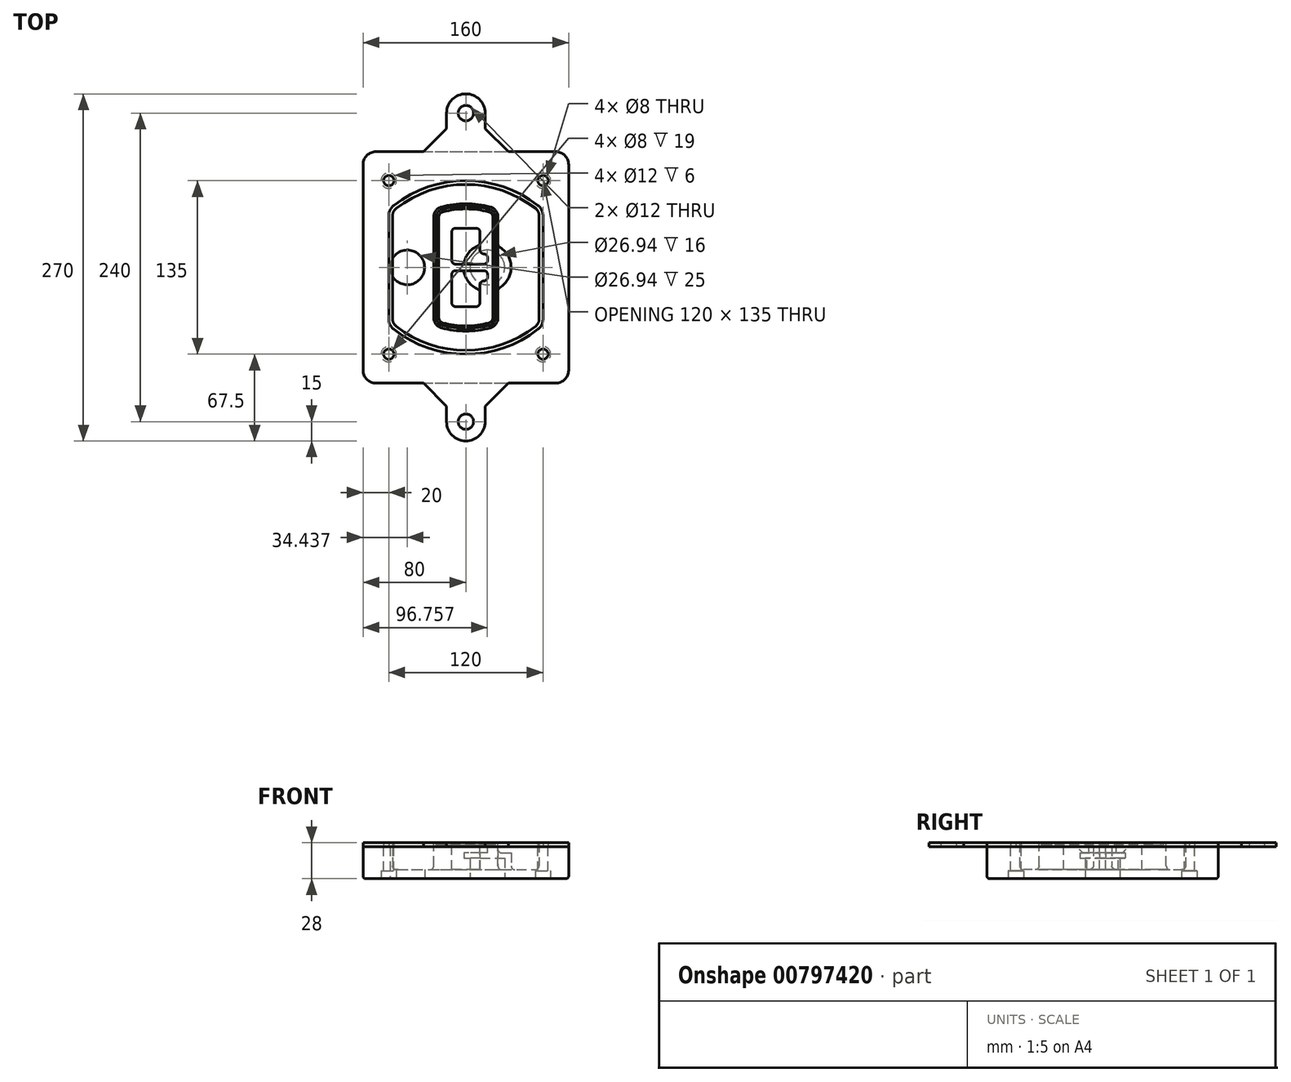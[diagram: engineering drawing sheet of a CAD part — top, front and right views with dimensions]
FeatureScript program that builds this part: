
annotation { "Feature Type Name" : "Feature", "Feature Type Description" : "" }
export const myFeature = defineFeature(function(context is Context, id is Id, definition is map)
    precondition{}
    {
        {
            var Q0;
            Q0=qCreatedBy(makeId("Top.planeOp"),FACE);
            var sketch = newSketch(context, id + "F0", { "sketchPlane" : qUnion([Q0])});
            skPoint(sketch, "E0.rect.middle", {"position": v(0, 0) * mm});
            skLineSegment(sketch, "E1.bottom", {"start": v(-70, -90) * mm, "end": v(70, -90) * mm});
            skLineSegment(sketch, "E1.top", {"start": v(-70, 90) * mm, "end": v(70, 90) * mm});
            skLineSegment(sketch, "E1.left", {"start": v(-80, -80) * mm, "end": v(-80, 80) * mm});
            skLineSegment(sketch, "E1.right", {"start": v(80, -80) * mm, "end": v(80, 80) * mm});
            skLineSegment(sketch, "E2", {"start": v(-80, 90) * mm, "end": v(80, -90) * mm, "construction": true});
            skLineSegment(sketch, "E3", {"start": v(80, 90) * mm, "end": v(-80, -90) * mm, "construction": true});
            skCircle(sketch, "E4", {"center": v(-60, 67.5) * mm, "radius": 4 * mm});
            skCircle(sketch, "E5", {"center": v(60, 67.5) * mm, "radius": 4 * mm});
            skCircle(sketch, "E6", {"center": v(60, -67.5) * mm, "radius": 4 * mm});
            skCircle(sketch, "E7", {"center": v(-60, -67.5) * mm, "radius": 4 * mm});
            skLineSegment(sketch, "E8", {"start": v(-60, 67.5) * mm, "end": v(60, 67.5) * mm, "construction": true});
            skLineSegment(sketch, "E9", {"start": v(60, 67.5) * mm, "end": v(60, -67.5) * mm, "construction": true});
            skLineSegment(sketch, "E10", {"start": v(60, -67.5) * mm, "end": v(-60, -67.5) * mm, "construction": true});
            skLineSegment(sketch, "E11", {"start": v(-60, -67.5) * mm, "end": v(-60, 67.5) * mm, "construction": true});
            skLineSegment(sketch, "E12", {"start": v(-60, 40.3) * mm, "end": v(-60, -40.3) * mm});
            skLineSegment(sketch, "E13", {"start": v(60, 40.3) * mm, "end": v(60, -40.3) * mm});
            skArc(sketch, "E14", {"start": v(56.15, 48.18) * mm, "mid": v(0, 67.5) * mm, "end": v(-56.15, 48.18) * mm});
            skArc(sketch, "E15", {"start": v(-56.15, -48.18) * mm, "mid": v(0, -67.5) * mm, "end": v(56.15, -48.18) * mm});
            skLineSegment(sketch, "E16", {"start": v(-60, 0) * mm, "end": v(60, 0) * mm, "construction": true});
            skPoint(sketch, "E17.visualSharp", {"position": v(-60, -45) * mm});
            skArc(sketch, "E17.filletArc", {"start": v(-60, -40.3) * mm, "mid": v(-58.99, -44.68) * mm, "end": v(-56.15, -48.18) * mm});
            skPoint(sketch, "E18.visualSharp", {"position": v(-60, 45) * mm});
            skArc(sketch, "E18.filletArc", {"start": v(-56.15, 48.18) * mm, "mid": v(-58.99, 44.68) * mm, "end": v(-60, 40.3) * mm});
            skPoint(sketch, "E19.visualSharp", {"position": v(60, 45) * mm});
            skArc(sketch, "E19.filletArc", {"start": v(60, 40.3) * mm, "mid": v(58.99, 44.68) * mm, "end": v(56.15, 48.18) * mm});
            skPoint(sketch, "E20.visualSharp", {"position": v(60, -45) * mm});
            skArc(sketch, "E20.filletArc", {"start": v(56.15, -48.18) * mm, "mid": v(58.99, -44.68) * mm, "end": v(60, -40.3) * mm});
            skPoint(sketch, "E21.visualSharp", {"position": v(-80, 90) * mm});
            skArc(sketch, "E21.filletArc", {"start": v(-70, 90) * mm, "mid": v(-77.07, 87.07) * mm, "end": v(-80, 80) * mm});
            skPoint(sketch, "E22.visualSharp", {"position": v(80, 90) * mm});
            skArc(sketch, "E22.filletArc", {"start": v(80, 80) * mm, "mid": v(77.07, 87.07) * mm, "end": v(70, 90) * mm});
            skPoint(sketch, "E23.visualSharp", {"position": v(80, -90) * mm});
            skArc(sketch, "E23.filletArc", {"start": v(70, -90) * mm, "mid": v(77.07, -87.07) * mm, "end": v(80, -80) * mm});
            skPoint(sketch, "E24.visualSharp", {"position": v(-80, -90) * mm});
            skArc(sketch, "E24.filletArc", {"start": v(-80, -80) * mm, "mid": v(-77.07, -87.07) * mm, "end": v(-70, -90) * mm});
            skArc(sketch, "E25.0", {"start": v(57, 40.3) * mm, "mid": v(56.3, 43.36) * mm, "end": v(54.3, 45.81) * mm});
            skLineSegment(sketch, "E25.1", {"start": v(57, 40.3) * mm, "end": v(57, -40.3) * mm});
            skArc(sketch, "E25.2", {"start": v(54.3, -45.81) * mm, "mid": v(56.3, -43.36) * mm, "end": v(57, -40.3) * mm});
            skArc(sketch, "E25.3", {"start": v(-54.3, -45.81) * mm, "mid": v(0, -64.5) * mm, "end": v(54.3, -45.81) * mm});
            skArc(sketch, "E25.4", {"start": v(-57, -40.3) * mm, "mid": v(-56.3, -43.36) * mm, "end": v(-54.3, -45.81) * mm});
            skArc(sketch, "E25.5", {"start": v(54.3, 45.81) * mm, "mid": v(0, 64.5) * mm, "end": v(-54.3, 45.81) * mm});
            skLineSegment(sketch, "E25.6", {"start": v(-57, 40.3) * mm, "end": v(-57, -40.3) * mm});
            skArc(sketch, "E25.7", {"start": v(-54.3, 45.81) * mm, "mid": v(-56.3, 43.36) * mm, "end": v(-57, 40.3) * mm});
            skArc(sketch, "E26.0", {"start": v(-58.62, 51.33) * mm, "mid": v(-62.58, 46.43) * mm, "end": v(-64, 40.3) * mm});
            skArc(sketch, "E26.1", {"start": v(58.62, 51.33) * mm, "mid": v(0, 71.5) * mm, "end": v(-58.62, 51.33) * mm});
            skArc(sketch, "E26.2", {"start": v(64, 40.3) * mm, "mid": v(62.58, 46.43) * mm, "end": v(58.62, 51.33) * mm});
            skLineSegment(sketch, "E26.3", {"start": v(64, 40.3) * mm, "end": v(64, -40.3) * mm});
            skArc(sketch, "E26.4", {"start": v(58.62, -51.33) * mm, "mid": v(62.58, -46.43) * mm, "end": v(64, -40.3) * mm});
            skLineSegment(sketch, "E26.5", {"start": v(-64, 40.3) * mm, "end": v(-64, -40.3) * mm});
            skArc(sketch, "E26.6", {"start": v(-58.62, -51.33) * mm, "mid": v(0, -71.5) * mm, "end": v(58.62, -51.33) * mm});
            skArc(sketch, "E26.7", {"start": v(-64, -40.3) * mm, "mid": v(-62.58, -46.43) * mm, "end": v(-58.62, -51.33) * mm});
            skSolve(sketch);
        }
        {
            var Q0;
            Q0=makeQuery(id+"F0.imprint","IMPRINT",FACE,{"disambiguationData":[TD([[makeQuery(id+"F0.imprint","IMPRINT",EDGE,{"derivedFrom":sQuery(id+"F0.wireOp",EDGE,"E1.bottom")}),1.0]])]});
            var Q1;
            Q1=makeQuery(id+"F0.imprint","IMPRINT",FACE,{"disambiguationData":[TD([[makeQuery(id+"F0.imprint","IMPRINT",EDGE,{"derivedFrom":sQuery(id+"F0.wireOp",EDGE,"E12")}),1.0]])]});
            var Q2;
            Q2=makeQuery(id+"F0.imprint","IMPRINT",FACE,{"disambiguationData":[TD([[makeQuery(id+"F0.imprint","IMPRINT",EDGE,{"derivedFrom":sQuery(id+"F0.wireOp",EDGE,"E25.0")}),1.0]])]});
            var Q3;
            Q3=makeQuery(id+"F0.imprint","IMPRINT",FACE,{"disambiguationData":[TD([[makeQuery(id+"F0.imprint","IMPRINT",EDGE,{"derivedFrom":sQuery(id+"F0.wireOp",EDGE,"E12")}),-1.0]])]});
            extrude(context, id + "F1", {"entities" : qUnion([Q0, Q1, Q2, Q3]), "oppositeDirection" : true, "depth" : 25 * mm});
        }
        {
            var Q0;
            Q0=makeQuery(id+"F0.imprint","IMPRINT",FACE,{"disambiguationData":[TD([[makeQuery(id+"F0.imprint","IMPRINT",EDGE,{"derivedFrom":sQuery(id+"F0.wireOp",EDGE,"E12")}),1.0]])]});
            extrude(context, id + "F2", {"entities" : qUnion([Q0]), "operationType" : NewBodyOperationType.ADD, "depth" : 3 * mm});
        }
        {
            var Q0;
            Q0=makeQuery(id+"F0.imprint","IMPRINT",FACE,{"disambiguationData":[TD([[makeQuery(id+"F0.imprint","IMPRINT",EDGE,{"derivedFrom":sQuery(id+"F0.wireOp",EDGE,"E25.0")}),1.0]])]});
            extrude(context, id + "F3", {"entities" : qUnion([Q0]), "operationType" : NewBodyOperationType.REMOVE, "oppositeDirection" : true, "depth" : 18 * mm});
        }
        {
            var Q0;
            Q0=makeQuery(id+"F2.opExtrude","CAP_FACE",FACE,{"disambiguationData":[OSD([sQuery(id+"F0.wireOp",EDGE,"E12"),sQuery(id+"F0.wireOp",EDGE,"E13"),sQuery(id+"F0.wireOp",EDGE,"E14"),sQuery(id+"F0.wireOp",EDGE,"E15"),sQuery(id+"F0.wireOp",EDGE,"E17.filletArc"),sQuery(id+"F0.wireOp",EDGE,"E18.filletArc"),sQuery(id+"F0.wireOp",EDGE,"E19.filletArc"),sQuery(id+"F0.wireOp",EDGE,"E20.filletArc"),sQuery(id+"F0.wireOp",EDGE,"E25.0"),sQuery(id+"F0.wireOp",EDGE,"E25.1"),sQuery(id+"F0.wireOp",EDGE,"E25.2"),sQuery(id+"F0.wireOp",EDGE,"E25.3"),sQuery(id+"F0.wireOp",EDGE,"E25.4"),sQuery(id+"F0.wireOp",EDGE,"E25.5"),sQuery(id+"F0.wireOp",EDGE,"E25.6"),sQuery(id+"F0.wireOp",EDGE,"E25.7")])],"isStart":false});
            var sketch = newSketch(context, id + "F4", { "sketchPlane" : qUnion([Q0])});
            skArc(sketch, "E27.0", {"start": v(-19.08, -46.97) * mm, "mid": v(0, -49.5) * mm, "end": v(19.08, -46.97) * mm});
            skArc(sketch, "E28.0", {"start": v(19.08, 46.97) * mm, "mid": v(0, 49.5) * mm, "end": v(-19.08, 46.97) * mm});
            skLineSegment(sketch, "E29", {"start": v(-25, 39.25) * mm, "end": v(-25, -39.25) * mm});
            skLineSegment(sketch, "E30", {"start": v(25, 39.25) * mm, "end": v(25, -39.25) * mm});
            skLineSegment(sketch, "E31", {"start": v(-25, 45.1) * mm, "end": v(25, 45.1) * mm, "construction": true});
            skLineSegment(sketch, "E32", {"start": v(-25, -45.1) * mm, "end": v(25, -45.1) * mm, "construction": true});
            skPoint(sketch, "E33.visualSharp", {"position": v(-25, 45.1) * mm});
            skArc(sketch, "E33.filletArc", {"start": v(-19.08, 46.97) * mm, "mid": v(-23.35, 44.11) * mm, "end": v(-25, 39.25) * mm});
            skPoint(sketch, "E34.visualSharp", {"position": v(25, 45.1) * mm});
            skArc(sketch, "E34.filletArc", {"start": v(25, 39.25) * mm, "mid": v(23.35, 44.11) * mm, "end": v(19.08, 46.97) * mm});
            skPoint(sketch, "E35.visualSharp", {"position": v(25, -45.1) * mm});
            skArc(sketch, "E35.filletArc", {"start": v(19.08, -46.97) * mm, "mid": v(23.35, -44.11) * mm, "end": v(25, -39.25) * mm});
            skPoint(sketch, "E36.visualSharp", {"position": v(-25, -45.1) * mm});
            skArc(sketch, "E36.filletArc", {"start": v(-25, -39.25) * mm, "mid": v(-23.35, -44.11) * mm, "end": v(-19.08, -46.97) * mm});
            skArc(sketch, "E37.0", {"start": v(54.3, 45.81) * mm, "mid": v(0, 64.5) * mm, "end": v(-54.3, 45.81) * mm});
            skArc(sketch, "E37.1", {"start": v(-54.3, 45.81) * mm, "mid": v(-56.3, 43.36) * mm, "end": v(-57, 40.3) * mm});
            skLineSegment(sketch, "E37.2", {"start": v(-57, 40.3) * mm, "end": v(-57, -40.3) * mm});
            skArc(sketch, "E37.3", {"start": v(-57, -40.3) * mm, "mid": v(-56.3, -43.36) * mm, "end": v(-54.3, -45.81) * mm});
            skArc(sketch, "E37.4", {"start": v(-54.3, -45.81) * mm, "mid": v(0, -64.5) * mm, "end": v(54.3, -45.81) * mm});
            skArc(sketch, "E37.5", {"start": v(54.3, -45.81) * mm, "mid": v(56.3, -43.36) * mm, "end": v(57, -40.3) * mm});
            skLineSegment(sketch, "E37.6", {"start": v(57, 40.3) * mm, "end": v(57, -40.3) * mm});
            skArc(sketch, "E37.7", {"start": v(57, 40.3) * mm, "mid": v(56.3, 43.36) * mm, "end": v(54.3, 45.81) * mm});
            skLineSegment(sketch, "E38.0", {"start": v(23, 39.25) * mm, "end": v(23, -39.25) * mm});
            skArc(sketch, "E38.1", {"start": v(18.56, -45.04) * mm, "mid": v(21.76, -42.9) * mm, "end": v(23, -39.25) * mm});
            skArc(sketch, "E38.2", {"start": v(-18.56, -45.04) * mm, "mid": v(0, -47.5) * mm, "end": v(18.56, -45.04) * mm});
            skArc(sketch, "E38.3", {"start": v(-23, -39.25) * mm, "mid": v(-21.76, -42.9) * mm, "end": v(-18.56, -45.04) * mm});
            skLineSegment(sketch, "E38.4", {"start": v(-23, 39.25) * mm, "end": v(-23, -39.25) * mm});
            skArc(sketch, "E38.5", {"start": v(23, 39.25) * mm, "mid": v(21.76, 42.9) * mm, "end": v(18.56, 45.04) * mm});
            skArc(sketch, "E38.6", {"start": v(-18.56, 45.04) * mm, "mid": v(-21.76, 42.9) * mm, "end": v(-23, 39.25) * mm});
            skArc(sketch, "E38.7", {"start": v(18.56, 45.04) * mm, "mid": v(0, 47.5) * mm, "end": v(-18.56, 45.04) * mm});
            skArc(sketch, "E39.0", {"start": v(21, 39.25) * mm, "mid": v(20.18, 41.68) * mm, "end": v(18.04, 43.1) * mm});
            skLineSegment(sketch, "E39.1", {"start": v(21, 39.25) * mm, "end": v(21, -39.25) * mm});
            skArc(sketch, "E39.2", {"start": v(18.04, -43.1) * mm, "mid": v(20.18, -41.68) * mm, "end": v(21, -39.25) * mm});
            skArc(sketch, "E39.3", {"start": v(-18.04, -43.1) * mm, "mid": v(0, -45.5) * mm, "end": v(18.04, -43.1) * mm});
            skArc(sketch, "E39.4", {"start": v(-21, -39.25) * mm, "mid": v(-20.18, -41.68) * mm, "end": v(-18.04, -43.1) * mm});
            skArc(sketch, "E39.5", {"start": v(18.04, 43.1) * mm, "mid": v(0, 45.5) * mm, "end": v(-18.04, 43.1) * mm});
            skLineSegment(sketch, "E39.6", {"start": v(-21, 39.25) * mm, "end": v(-21, -39.25) * mm});
            skArc(sketch, "E39.7", {"start": v(-18.04, 43.1) * mm, "mid": v(-20.18, 41.68) * mm, "end": v(-21, 39.25) * mm});
            skLineSegment(sketch, "E40", {"start": v(-25, 0) * mm, "end": v(25, 0) * mm, "construction": true});
            skLineSegment(sketch, "E41", {"start": v(-11, 5.5) * mm, "end": v(-11, 27.5) * mm});
            skLineSegment(sketch, "E42", {"start": v(-8, 30.5) * mm, "end": v(8, 30.5) * mm});
            skLineSegment(sketch, "E43", {"start": v(11, 27.5) * mm, "end": v(11, 13.5) * mm});
            skLineSegment(sketch, "E44", {"start": v(14, 10.5) * mm, "end": v(14, 10.5) * mm});
            skLineSegment(sketch, "E45", {"start": v(17, 7.5) * mm, "end": v(17, 5.5) * mm});
            skLineSegment(sketch, "E46", {"start": v(14, 2.5) * mm, "end": v(-8, 2.5) * mm});
            skPoint(sketch, "E47.visualSharp", {"position": v(-11, 30.5) * mm});
            skArc(sketch, "E47.filletArc", {"start": v(-8, 30.5) * mm, "mid": v(-10.12, 29.62) * mm, "end": v(-11, 27.5) * mm});
            skPoint(sketch, "E48.visualSharp", {"position": v(11, 30.5) * mm});
            skArc(sketch, "E48.filletArc", {"start": v(11, 27.5) * mm, "mid": v(10.12, 29.62) * mm, "end": v(8, 30.5) * mm});
            skPoint(sketch, "E49.visualSharp", {"position": v(11, 10.5) * mm});
            skArc(sketch, "E49.filletArc", {"start": v(11, 13.5) * mm, "mid": v(11.88, 11.38) * mm, "end": v(14, 10.5) * mm});
            skPoint(sketch, "E50.visualSharp", {"position": v(17, 10.5) * mm});
            skArc(sketch, "E50.filletArc", {"start": v(17, 7.5) * mm, "mid": v(16.12, 9.62) * mm, "end": v(14, 10.5) * mm});
            skPoint(sketch, "E51.visualSharp", {"position": v(17, 2.5) * mm});
            skArc(sketch, "E51.filletArc", {"start": v(14, 2.5) * mm, "mid": v(16.12, 3.38) * mm, "end": v(17, 5.5) * mm});
            skPoint(sketch, "E52.visualSharp", {"position": v(-11, 2.5) * mm});
            skArc(sketch, "E52.filletArc", {"start": v(-11, 5.5) * mm, "mid": v(-10.12, 3.38) * mm, "end": v(-8, 2.5) * mm});
            skLineSegment(sketch, "E53.0.MirrorCS", {"start": v(14, -2.5) * mm, "end": v(-8, -2.5) * mm});
            skArc(sketch, "E54.0.MirrorCS", {"start": v(-11, -5.5) * mm, "mid": v(-10.12, -3.38) * mm, "end": v(-8, -2.5) * mm});
            skLineSegment(sketch, "E55.0.MirrorCS", {"start": v(-11, -5.5) * mm, "end": v(-11, -27.5) * mm});
            skArc(sketch, "E56.0.MirrorCS", {"start": v(-8, -30.5) * mm, "mid": v(-10.12, -29.62) * mm, "end": v(-11, -27.5) * mm});
            skLineSegment(sketch, "E57.0.MirrorCS", {"start": v(-8, -30.5) * mm, "end": v(8, -30.5) * mm});
            skArc(sketch, "E58.0.MirrorCS", {"start": v(11, -27.5) * mm, "mid": v(10.12, -29.62) * mm, "end": v(8, -30.5) * mm});
            skLineSegment(sketch, "E59.0.MirrorCS", {"start": v(11, -27.5) * mm, "end": v(11, -13.5) * mm});
            skArc(sketch, "E60.0.MirrorCS", {"start": v(11, -13.5) * mm, "mid": v(11.88, -11.38) * mm, "end": v(14, -10.5) * mm});
            skArc(sketch, "E61.0.MirrorCS", {"start": v(17, -7.5) * mm, "mid": v(16.12, -9.62) * mm, "end": v(14, -10.5) * mm});
            skLineSegment(sketch, "E62.0.MirrorCS", {"start": v(17, -7.5) * mm, "end": v(17, -5.5) * mm});
            skArc(sketch, "E63.0.MirrorCS", {"start": v(14, -2.5) * mm, "mid": v(16.12, -3.38) * mm, "end": v(17, -5.5) * mm});
            skSolve(sketch);
        }
        {
            var Q0;
            Q0=makeQuery(id+"F4.imprint","IMPRINT",FACE,{"disambiguationData":[TD([[makeQuery(id+"F4.imprint","IMPRINT",EDGE,{"derivedFrom":sQuery(id+"F4.wireOp",EDGE,"E27.0")}),1.0]])]});
            var Q1;
            Q1=makeQuery(id+"F4.imprint","IMPRINT",FACE,{"disambiguationData":[TD([[makeQuery(id+"F4.imprint","IMPRINT",EDGE,{"derivedFrom":sQuery(id+"F4.wireOp",EDGE,"E38.0")}),-1.0]])]});
            var Q2;
            Q2=makeQuery(id+"F4.imprint","IMPRINT",FACE,{"disambiguationData":[TD([[makeQuery(id+"F4.imprint","IMPRINT",EDGE,{"derivedFrom":sQuery(id+"F4.wireOp",EDGE,"E39.0")}),1.0]])]});
            extrude(context, id + "F5", {"entities" : qUnion([Q0, Q1, Q2]), "operationType" : NewBodyOperationType.ADD, "endBound" : BoundingType.UP_TO_NEXT, "oppositeDirection" : true, "depth" : 25 * mm});
        }
        {
            var Q0;
            Q0=makeQuery(id+"F4.imprint","IMPRINT",FACE,{"disambiguationData":[TD([[makeQuery(id+"F4.imprint","IMPRINT",EDGE,{"derivedFrom":sQuery(id+"F4.wireOp",EDGE,"E38.0")}),-1.0]])]});
            extrude(context, id + "F6", {"entities" : qUnion([Q0]), "operationType" : NewBodyOperationType.REMOVE, "oppositeDirection" : true, "depth" : 2 * mm});
        }
        {
            var Q0;
            Q0=makeQuery(id+"F1.opExtrude","CAP_FACE",FACE,{"disambiguationData":[OSD([sQuery(id+"F0.wireOp",EDGE,"E1.bottom"),sQuery(id+"F0.wireOp",EDGE,"E1.top"),sQuery(id+"F0.wireOp",EDGE,"E1.left"),sQuery(id+"F0.wireOp",EDGE,"E1.right"),sQuery(id+"F0.wireOp",EDGE,"E4"),sQuery(id+"F0.wireOp",EDGE,"E5"),sQuery(id+"F0.wireOp",EDGE,"E6"),sQuery(id+"F0.wireOp",EDGE,"E7"),sQuery(id+"F0.wireOp",EDGE,"E21.filletArc"),sQuery(id+"F0.wireOp",EDGE,"E22.filletArc"),sQuery(id+"F0.wireOp",EDGE,"E23.filletArc"),sQuery(id+"F0.wireOp",EDGE,"E24.filletArc")])],"isStart":false});
            var sketch = newSketch(context, id + "F7", { "sketchPlane" : qUnion([Q0])});
            skCircle(sketch, "E64", {"center": v(16.76, 0) * mm, "radius": 13.47 * mm});
            skCircle(sketch, "E65", {"center": v(-45.56, 0) * mm, "radius": 13.47 * mm});
            skLineSegment(sketch, "E66", {"start": v(80, 0) * mm, "end": v(-80, 0) * mm});
            skCircle(sketch, "E67", {"center": v(16.76, 0) * mm, "radius": 18.47 * mm});
            skCircle(sketch, "E68", {"center": v(60, -67.5) * mm, "radius": 6 * mm});
            skCircle(sketch, "E69", {"center": v(-60, -67.5) * mm, "radius": 6 * mm});
            skCircle(sketch, "E70", {"center": v(-60, 67.5) * mm, "radius": 6 * mm});
            skCircle(sketch, "E71", {"center": v(60, 67.5) * mm, "radius": 6 * mm});
            skSolve(sketch);
        }
        {
            var Q0;
            {var subQ1=sQuery(id+"F7.wireOp",EDGE,"E66");var subQ4=sQuery(id+"F7.wireOp",EDGE,"E64");var subQ6=makeQuery(id+"F7.imprint","INTERSECT",VERTEX,{"disambiguationData":[OD(0.0)],"derivedFrom":[subQ4,subQ1]});Q0=makeQuery(id+"F7.imprint","IMPRINT",FACE,{"disambiguationData":[TD([[makeQuery(id+"F7.imprint","IMPRINT",EDGE,{"disambiguationData":[TD([[subQ6,-1.0]])],"derivedFrom":subQ4}),-1.0]])]});}
            var Q1;
            {var subQ0=sQuery(id+"F7.wireOp",EDGE,"E66");var subQ1=sQuery(id+"F7.wireOp",EDGE,"E64");var subQ3=makeQuery(id+"F7.imprint","INTERSECT",VERTEX,{"disambiguationData":[OD(0.0)],"derivedFrom":[subQ1,subQ0]});Q1=makeQuery(id+"F7.imprint","IMPRINT",FACE,{"disambiguationData":[TD([[makeQuery(id+"F7.imprint","IMPRINT",EDGE,{"disambiguationData":[TD([[subQ3,-1.0]])],"derivedFrom":subQ1}),1.0]])]});}
            var Q2;
            {var subQ0=sQuery(id+"F7.wireOp",EDGE,"E66");var subQ1=sQuery(id+"F7.wireOp",EDGE,"E64");var subQ3=makeQuery(id+"F7.imprint","INTERSECT",VERTEX,{"disambiguationData":[OD(0.0)],"derivedFrom":[subQ1,subQ0]});Q2=makeQuery(id+"F7.imprint","IMPRINT",FACE,{"disambiguationData":[TD([[makeQuery(id+"F7.imprint","IMPRINT",EDGE,{"disambiguationData":[TD([[subQ3,1.0]])],"derivedFrom":subQ1}),1.0]])]});}
            var Q3;
            {var subQ1=sQuery(id+"F7.wireOp",EDGE,"E66");var subQ4=sQuery(id+"F7.wireOp",EDGE,"E64");var subQ6=makeQuery(id+"F7.imprint","INTERSECT",VERTEX,{"disambiguationData":[OD(0.0)],"derivedFrom":[subQ4,subQ1]});Q3=makeQuery(id+"F7.imprint","IMPRINT",FACE,{"disambiguationData":[TD([[makeQuery(id+"F7.imprint","IMPRINT",EDGE,{"disambiguationData":[TD([[subQ6,1.0]])],"derivedFrom":subQ4}),-1.0]])]});}
            extrude(context, id + "F8", {"entities" : qUnion([Q0, Q1, Q2, Q3]), "operationType" : NewBodyOperationType.ADD, "oppositeDirection" : true, "depth" : 20 * mm});
        }
        {
            var Q0;
            {var subQ0=sQuery(id+"F7.wireOp",EDGE,"E66");var subQ1=sQuery(id+"F7.wireOp",EDGE,"E64");var subQ3=makeQuery(id+"F7.imprint","INTERSECT",VERTEX,{"disambiguationData":[OD(0.0)],"derivedFrom":[subQ1,subQ0]});Q0=makeQuery(id+"F7.imprint","IMPRINT",FACE,{"disambiguationData":[TD([[makeQuery(id+"F7.imprint","IMPRINT",EDGE,{"disambiguationData":[TD([[subQ3,-1.0]])],"derivedFrom":subQ1}),1.0]])]});}
            var Q1;
            {var subQ0=sQuery(id+"F7.wireOp",EDGE,"E66");var subQ1=sQuery(id+"F7.wireOp",EDGE,"E64");var subQ3=makeQuery(id+"F7.imprint","INTERSECT",VERTEX,{"disambiguationData":[OD(0.0)],"derivedFrom":[subQ1,subQ0]});Q1=makeQuery(id+"F7.imprint","IMPRINT",FACE,{"disambiguationData":[TD([[makeQuery(id+"F7.imprint","IMPRINT",EDGE,{"disambiguationData":[TD([[subQ3,1.0]])],"derivedFrom":subQ1}),1.0]])]});}
            extrude(context, id + "F9", {"entities" : qUnion([Q0, Q1]), "operationType" : NewBodyOperationType.REMOVE, "oppositeDirection" : true, "depth" : 16 * mm});
        }
        {
            var Q0;
            {var subQ0=sQuery(id+"F7.wireOp",EDGE,"E66");var subQ1=sQuery(id+"F7.wireOp",EDGE,"E65");var subQ3=makeQuery(id+"F7.imprint","INTERSECT",VERTEX,{"disambiguationData":[OD(0.0)],"derivedFrom":[subQ1,subQ0]});Q0=makeQuery(id+"F7.imprint","IMPRINT",FACE,{"disambiguationData":[TD([[makeQuery(id+"F7.imprint","IMPRINT",EDGE,{"disambiguationData":[TD([[subQ3,-1.0]])],"derivedFrom":subQ1}),1.0]])]});}
            var Q1;
            {var subQ0=sQuery(id+"F7.wireOp",EDGE,"E66");var subQ1=sQuery(id+"F7.wireOp",EDGE,"E65");var subQ3=makeQuery(id+"F7.imprint","INTERSECT",VERTEX,{"disambiguationData":[OD(0.0)],"derivedFrom":[subQ1,subQ0]});Q1=makeQuery(id+"F7.imprint","IMPRINT",FACE,{"disambiguationData":[TD([[makeQuery(id+"F7.imprint","IMPRINT",EDGE,{"disambiguationData":[TD([[subQ3,1.0]])],"derivedFrom":subQ1}),1.0]])]});}
            extrude(context, id + "F10", {"entities" : qUnion([Q0, Q1]), "operationType" : NewBodyOperationType.REMOVE, "oppositeDirection" : true, "depth" : 25 * mm});
        }
        {
            var Q0;
            Q0=makeQuery(id+"F7.imprint","IMPRINT",FACE,{"disambiguationData":[TD([[makeQuery(id+"F7.imprint","IMPRINT",EDGE,{"derivedFrom":sQuery(id+"F7.wireOp",EDGE,"E68")}),1.0]])]});
            var Q1;
            Q1=makeQuery(id+"F7.imprint","IMPRINT",FACE,{"disambiguationData":[TD([[makeQuery(id+"F7.imprint","IMPRINT",EDGE,{"derivedFrom":makeQuery(id+"F1.opExtrude","CAP_EDGE",EDGE,{"disambiguationData":[OSD([sQuery(id+"F0.wireOp",EDGE,"E5")])],"isStart":false})}),-1.0]])]});
            var Q2;
            Q2=makeQuery(id+"F7.imprint","IMPRINT",FACE,{"disambiguationData":[TD([[makeQuery(id+"F7.imprint","IMPRINT",EDGE,{"derivedFrom":sQuery(id+"F7.wireOp",EDGE,"E69")}),1.0]])]});
            var Q3;
            Q3=makeQuery(id+"F7.imprint","IMPRINT",FACE,{"disambiguationData":[TD([[makeQuery(id+"F7.imprint","IMPRINT",EDGE,{"derivedFrom":makeQuery(id+"F1.opExtrude","CAP_EDGE",EDGE,{"disambiguationData":[OSD([sQuery(id+"F0.wireOp",EDGE,"E4")])],"isStart":false})}),-1.0]])]});
            var Q4;
            Q4=makeQuery(id+"F7.imprint","IMPRINT",FACE,{"disambiguationData":[TD([[makeQuery(id+"F7.imprint","IMPRINT",EDGE,{"derivedFrom":sQuery(id+"F7.wireOp",EDGE,"E70")}),1.0]])]});
            var Q5;
            Q5=makeQuery(id+"F7.imprint","IMPRINT",FACE,{"disambiguationData":[TD([[makeQuery(id+"F7.imprint","IMPRINT",EDGE,{"derivedFrom":makeQuery(id+"F1.opExtrude","CAP_EDGE",EDGE,{"disambiguationData":[OSD([sQuery(id+"F0.wireOp",EDGE,"E7")])],"isStart":false})}),-1.0]])]});
            var Q6;
            Q6=makeQuery(id+"F7.imprint","IMPRINT",FACE,{"disambiguationData":[TD([[makeQuery(id+"F7.imprint","IMPRINT",EDGE,{"derivedFrom":sQuery(id+"F7.wireOp",EDGE,"E71")}),1.0]])]});
            var Q7;
            Q7=makeQuery(id+"F7.imprint","IMPRINT",FACE,{"disambiguationData":[TD([[makeQuery(id+"F7.imprint","IMPRINT",EDGE,{"derivedFrom":makeQuery(id+"F1.opExtrude","CAP_EDGE",EDGE,{"disambiguationData":[OSD([sQuery(id+"F0.wireOp",EDGE,"E6")])],"isStart":false})}),-1.0]])]});
            extrude(context, id + "F11", {"entities" : qUnion([Q0, Q1, Q2, Q3, Q4, Q5, Q6, Q7]), "operationType" : NewBodyOperationType.REMOVE, "oppositeDirection" : true, "depth" : 6 * mm});
        }
        {
            var Q0;
            Q0=makeQuery(id+"F9.boolean.opBoolean","COPY",FACE,{"derivedFrom":makeQuery(id+"F9.opExtrude","CAP_FACE",FACE,{"disambiguationData":[OSD([sQuery(id+"F7.wireOp",EDGE,"E64")])],"isStart":false})});
            var sketch = newSketch(context, id + "F12", { "sketchPlane" : qUnion([Q0])});
            skArc(sketch, "E72.0", {"start": v(11, 17.55) * mm, "mid": v(2.57, 11.82) * mm, "end": v(-1.54, 2.5) * mm});
            skArc(sketch, "E72.1", {"start": v(-1.54, -2.5) * mm, "mid": v(2.57, -11.82) * mm, "end": v(11, -17.55) * mm});
            skLineSegment(sketch, "E73", {"start": v(-1.54, -2.5) * mm, "end": v(14, -2.5) * mm});
            skLineSegment(sketch, "E74.0", {"start": v(14, 2.5) * mm, "end": v(-1.54, 2.5) * mm});
            skArc(sketch, "E74.1", {"start": v(14, 2.5) * mm, "mid": v(16.12, 3.38) * mm, "end": v(17, 5.5) * mm});
            skLineSegment(sketch, "E74.2", {"start": v(17, 7.5) * mm, "end": v(17, 5.5) * mm});
            skArc(sketch, "E74.3", {"start": v(17, 7.5) * mm, "mid": v(16.12, 9.62) * mm, "end": v(14, 10.5) * mm});
            skArc(sketch, "E74.4", {"start": v(11, 13.5) * mm, "mid": v(11.88, 11.38) * mm, "end": v(14, 10.5) * mm});
            skLineSegment(sketch, "E74.5", {"start": v(11, 17.55) * mm, "end": v(11, 13.5) * mm});
            skLineSegment(sketch, "E74.7", {"start": v(14, -2.5) * mm, "end": v(-1.54, -2.5) * mm});
            skArc(sketch, "E74.8", {"start": v(14, -2.5) * mm, "mid": v(16.12, -3.38) * mm, "end": v(17, -5.5) * mm});
            skLineSegment(sketch, "E74.9", {"start": v(17, -7.5) * mm, "end": v(17, -5.5) * mm});
            skArc(sketch, "E74.10", {"start": v(17, -7.5) * mm, "mid": v(16.12, -9.62) * mm, "end": v(14, -10.5) * mm});
            skArc(sketch, "E74.11", {"start": v(11, -13.5) * mm, "mid": v(11.88, -11.38) * mm, "end": v(14, -10.5) * mm});
            skLineSegment(sketch, "E74.12", {"start": v(11, -17.55) * mm, "end": v(11, -13.5) * mm});
            skPoint(sketch, "E75.orphan", {"position": v(11, -27.5) * mm});
            skPoint(sketch, "E76.orphan", {"position": v(-8, -2.5) * mm});
            skPoint(sketch, "E77.orphan", {"position": v(-8, 2.5) * mm});
            skPoint(sketch, "E78.orphan", {"position": v(11, 27.5) * mm});
            skSolve(sketch);
        }
        {
            var Q0;
            {var subQ7=sQuery(id+"F12.wireOp",EDGE,"E72.0");var subQ14=sQuery(id+"F12.wireOp",EDGE,"E72.1");var subQ16=sQuery(id+"F12.wireOp",EDGE,"E74.1");var subQ18=sQuery(id+"F12.wireOp",EDGE,"E74.8");Q0=qUnion([makeQuery(id+"F12.imprint","IMPRINT",FACE,{"disambiguationData":[TD([[makeQuery(id+"F12.imprint","IMPRINT",EDGE,{"derivedFrom":subQ7}),1.0]])]}),makeQuery(id+"F12.imprint","IMPRINT",FACE,{"disambiguationData":[TD([[makeQuery(id+"F12.imprint","IMPRINT",EDGE,{"derivedFrom":subQ14}),1.0]])]}),makeQuery(id+"F12.imprint","IMPRINT",FACE,{"disambiguationData":[TD([[makeQuery(id+"F12.imprint","IMPRINT",EDGE,{"derivedFrom":subQ16}),1.0]])]}),makeQuery(id+"F12.imprint","IMPRINT",FACE,{"disambiguationData":[TD([[makeQuery(id+"F12.imprint","IMPRINT",EDGE,{"derivedFrom":subQ18}),-1.0]])]})]);}
            var Q1;
            Q1=makeQuery(id+"F5.boolean.opBoolean","SPLIT",FACE,{"disambiguationData":[TD([makeQuery(id+"F5.opExtrude","SWEPT_FACE",FACE,{"disambiguationData":[OSD([sQuery(id+"F4.wireOp",EDGE,"E41")])]})])],"derivedFrom":makeQuery(id+"F3.boolean.opBoolean","COPY",FACE,{"derivedFrom":makeQuery(id+"F3.opExtrude","CAP_FACE",FACE,{"disambiguationData":[OSD([sQuery(id+"F0.wireOp",EDGE,"E25.0"),sQuery(id+"F0.wireOp",EDGE,"E25.1"),sQuery(id+"F0.wireOp",EDGE,"E25.2"),sQuery(id+"F0.wireOp",EDGE,"E25.3"),sQuery(id+"F0.wireOp",EDGE,"E25.4"),sQuery(id+"F0.wireOp",EDGE,"E25.5"),sQuery(id+"F0.wireOp",EDGE,"E25.6"),sQuery(id+"F0.wireOp",EDGE,"E25.7")])],"isStart":false})})});
            extrude(context, id + "F13", {"entities" : qUnion([Q0]), "operationType" : NewBodyOperationType.REMOVE, "endBound" : BoundingType.UP_TO_SURFACE, "endBoundEntityFace" : qUnion([Q1]), "depth" : 25 * mm});
        }
        {
            var Q0;
            Q0=makeQuery(id+"F3.boolean.opBoolean","COPY",EDGE,{"derivedFrom":makeQuery(id+"F3.opExtrude","CAP_EDGE",EDGE,{"disambiguationData":[OSD([sQuery(id+"F0.wireOp",EDGE,"E25.6")])],"isStart":false})});
            var Q1;
            Q1=makeQuery(id+"F8.boolean.opBoolean","INTERSECT",EDGE,{"derivedFrom":[makeQuery(id+"F5.opExtrude","SWEPT_FACE",FACE,{"disambiguationData":[OSD([sQuery(id+"F4.wireOp",EDGE,"E30")])]}),makeQuery(id+"F8.opExtrude","CAP_FACE",FACE,{"disambiguationData":[OSD([sQuery(id+"F7.wireOp",EDGE,"E67")])],"isStart":false})]});
            var Q2;
            Q2=makeQuery(id+"F8.boolean.opBoolean","INTERSECT",EDGE,{"disambiguationData":[OD(1.0)],"derivedFrom":[makeQuery(id+"F5.opExtrude","SWEPT_FACE",FACE,{"disambiguationData":[OSD([sQuery(id+"F4.wireOp",EDGE,"E30")])]}),makeQuery(id+"F8.opExtrude","SWEPT_FACE",FACE,{"disambiguationData":[OSD([sQuery(id+"F7.wireOp",EDGE,"E67")])]})]});
            var Q3;
            {var subQ0=sQuery(id+"F4.wireOp",EDGE,"E30");Q3=makeQuery(id+"F8.boolean.opBoolean","SPLIT",EDGE,{"disambiguationData":[TD([makeQuery(id+"F5.opExtrude","SWEPT_FACE",FACE,{"disambiguationData":[OSD([sQuery(id+"F4.wireOp",EDGE,"E35.filletArc")])]})])],"derivedFrom":makeQuery(id+"F5.opExtrude","CAP_EDGE",EDGE,{"disambiguationData":[OSD([subQ0])],"isStart":false})});}
            var Q4;
            {var subQ0=sQuery(id+"F0.wireOp",EDGE,"E25.7");var subQ1=sQuery(id+"F0.wireOp",EDGE,"E25.1");var subQ2=sQuery(id+"F0.wireOp",EDGE,"E25.6");var subQ3=sQuery(id+"F0.wireOp",EDGE,"E25.5");var subQ4=sQuery(id+"F0.wireOp",EDGE,"E25.4");var subQ5=sQuery(id+"F0.wireOp",EDGE,"E25.0");var subQ6=sQuery(id+"F0.wireOp",EDGE,"E25.2");var subQ7=sQuery(id+"F0.wireOp",EDGE,"E25.3");Q4=makeQuery(id+"F8.boolean.opBoolean","INTERSECT",EDGE,{"derivedFrom":[makeQuery(id+"F5.boolean.opBoolean","SPLIT",FACE,{"disambiguationData":[TD([makeQuery(id+"F2.opExtrude","SWEPT_FACE",FACE,{"disambiguationData":[OSD([subQ5])]})])],"derivedFrom":makeQuery(id+"F3.boolean.opBoolean","COPY",FACE,{"derivedFrom":makeQuery(id+"F3.opExtrude","CAP_FACE",FACE,{"disambiguationData":[OSD([subQ5,subQ1,subQ6,subQ7,subQ4,subQ3,subQ2,subQ0])],"isStart":false})})}),makeQuery(id+"F8.opExtrude","SWEPT_FACE",FACE,{"disambiguationData":[OSD([sQuery(id+"F7.wireOp",EDGE,"E67")])]})]});}
            var Q5;
            Q5=makeQuery(id+"F8.boolean.opBoolean","INTERSECT",EDGE,{"disambiguationData":[OD(0.0)],"derivedFrom":[makeQuery(id+"F5.opExtrude","SWEPT_FACE",FACE,{"disambiguationData":[OSD([sQuery(id+"F4.wireOp",EDGE,"E30")])]}),makeQuery(id+"F8.opExtrude","SWEPT_FACE",FACE,{"disambiguationData":[OSD([sQuery(id+"F7.wireOp",EDGE,"E67")])]})]});
            fillet(context, id + "F14", {"entities" : qUnion([Q0, Q1, Q2, Q3, Q4, Q5]), "radius" : 3 * mm, "tangentPropagation" : true, "allowEdgeOverflow" : false});
        }
        {
            var Q0;
            Q0=makeQuery(id+"F1.opExtrude","CAP_EDGE",EDGE,{"disambiguationData":[OSD([sQuery(id+"F0.wireOp",EDGE,"E1.bottom")])],"isStart":false});
            fillet(context, id + "F15", {"entities" : qUnion([Q0]), "radius" : 2 * mm, "tangentPropagation" : true, "allowEdgeOverflow" : false});
        }
        {
            var Q0;
            {var subQ0=sQuery(id+"F0.wireOp",EDGE,"E21.filletArc");var subQ1=sQuery(id+"F0.wireOp",EDGE,"E7");var subQ2=sQuery(id+"F0.wireOp",EDGE,"E6");var subQ3=sQuery(id+"F0.wireOp",EDGE,"E5");var subQ4=sQuery(id+"F0.wireOp",EDGE,"E4");var subQ5=sQuery(id+"F0.wireOp",EDGE,"E22.filletArc");var subQ6=sQuery(id+"F0.wireOp",EDGE,"E1.bottom");var subQ7=sQuery(id+"F0.wireOp",EDGE,"E1.right");var subQ8=sQuery(id+"F0.wireOp",EDGE,"E1.top");var subQ9=sQuery(id+"F0.wireOp",EDGE,"E1.left");var subQ10=sQuery(id+"F0.wireOp",EDGE,"E23.filletArc");var subQ11=sQuery(id+"F0.wireOp",EDGE,"E24.filletArc");Q0=makeQuery(id+"F2.boolean.opBoolean","SPLIT",FACE,{"disambiguationData":[TD([makeQuery(id+"F1.opExtrude","SWEPT_FACE",FACE,{"disambiguationData":[OSD([subQ6])]})])],"derivedFrom":makeQuery(id+"F1.opExtrude","CAP_FACE",FACE,{"disambiguationData":[OSD([subQ6,subQ8,subQ9,subQ7,subQ4,subQ3,subQ2,subQ1,subQ0,subQ5,subQ10,subQ11])],"isStart":true})});}
            var sketch = newSketch(context, id + "F16", { "sketchPlane" : qUnion([Q0])});
            skLineSegment(sketch, "E79", {"start": v(0, 90) * mm, "end": v(0, 120) * mm, "construction": true});
            skCircle(sketch, "E80", {"center": v(0, 120) * mm, "radius": 6 * mm});
            skArc(sketch, "E81", {"start": v(-15, 120) * mm, "mid": v(0, 135) * mm, "end": v(15, 120) * mm});
            skLineSegment(sketch, "E82", {"start": v(-15, 120) * mm, "end": v(-15, 108) * mm});
            skLineSegment(sketch, "E83", {"start": v(-15, 108) * mm, "end": v(-33, 90) * mm});
            skLineSegment(sketch, "E84.MirrorCS", {"start": v(15, 120) * mm, "end": v(15, 108) * mm});
            skLineSegment(sketch, "E85.MirrorCS", {"start": v(15, 108) * mm, "end": v(33, 90) * mm});
            skLineSegment(sketch, "E86", {"start": v(-80, 0) * mm, "end": v(80, 0) * mm, "construction": true});
            skLineSegment(sketch, "E87.MirrorCS", {"start": v(-15, -108) * mm, "end": v(-33, -90) * mm});
            skLineSegment(sketch, "E88.MirrorCS", {"start": v(-15, -120) * mm, "end": v(-15, -108) * mm});
            skArc(sketch, "E89.MirrorCS", {"start": v(-15, -120) * mm, "mid": v(0, -135) * mm, "end": v(15, -120) * mm});
            skCircle(sketch, "E90.MirrorC", {"center": v(0, -120) * mm, "radius": 6 * mm});
            skLineSegment(sketch, "E91.MirrorCS", {"start": v(15, -120) * mm, "end": v(15, -108) * mm});
            skLineSegment(sketch, "E92.MirrorCS", {"start": v(15, -108) * mm, "end": v(33, -90) * mm});
            skLineSegment(sketch, "E93.MirrorCS", {"start": v(0, -90) * mm, "end": v(0, -120) * mm, "construction": true});
            skSolve(sketch);
        }
        {
            var Q0;
            {var subQ0=sQuery(id+"F16.wireOp",EDGE,"E87.MirrorCS");Q0=makeQuery(id+"F16.imprint","IMPRINT",FACE,{"disambiguationData":[TD([[makeQuery(id+"F16.imprint","IMPRINT",EDGE,{"derivedFrom":subQ0}),-1.0]])]});}
            var Q1;
            Q1=makeQuery(id+"F16.imprint","IMPRINT",FACE,{"disambiguationData":[TD([[makeQuery(id+"F16.imprint","IMPRINT",EDGE,{"derivedFrom":makeQuery(id+"F1.opExtrude","CAP_EDGE",EDGE,{"disambiguationData":[OSD([sQuery(id+"F0.wireOp",EDGE,"E1.left")])],"isStart":true})}),-1.0]])]});
            var Q2;
            Q2=makeQuery(id+"F16.imprint","IMPRINT",FACE,{"disambiguationData":[TD([[makeQuery(id+"F16.imprint","IMPRINT",EDGE,{"derivedFrom":sQuery(id+"F16.wireOp",EDGE,"E80")}),-1.0]])]});
            var Q3;
            Q3=makeQuery(id+"F2.opExtrude","CAP_FACE",FACE,{"disambiguationData":[OSD([sQuery(id+"F0.wireOp",EDGE,"E12"),sQuery(id+"F0.wireOp",EDGE,"E13"),sQuery(id+"F0.wireOp",EDGE,"E14"),sQuery(id+"F0.wireOp",EDGE,"E15"),sQuery(id+"F0.wireOp",EDGE,"E17.filletArc"),sQuery(id+"F0.wireOp",EDGE,"E18.filletArc"),sQuery(id+"F0.wireOp",EDGE,"E19.filletArc"),sQuery(id+"F0.wireOp",EDGE,"E20.filletArc"),sQuery(id+"F0.wireOp",EDGE,"E25.0"),sQuery(id+"F0.wireOp",EDGE,"E25.1"),sQuery(id+"F0.wireOp",EDGE,"E25.2"),sQuery(id+"F0.wireOp",EDGE,"E25.3"),sQuery(id+"F0.wireOp",EDGE,"E25.4"),sQuery(id+"F0.wireOp",EDGE,"E25.5"),sQuery(id+"F0.wireOp",EDGE,"E25.6"),sQuery(id+"F0.wireOp",EDGE,"E25.7")])],"isStart":false});
            extrude(context, id + "F17", {"entities" : qUnion([Q0, Q1, Q2]), "endBound" : BoundingType.UP_TO_SURFACE, "depth" : 25 * mm, "endBoundEntityFace" : qUnion([Q3]), "offsetDistance" : 25 * mm});
        }
    });
